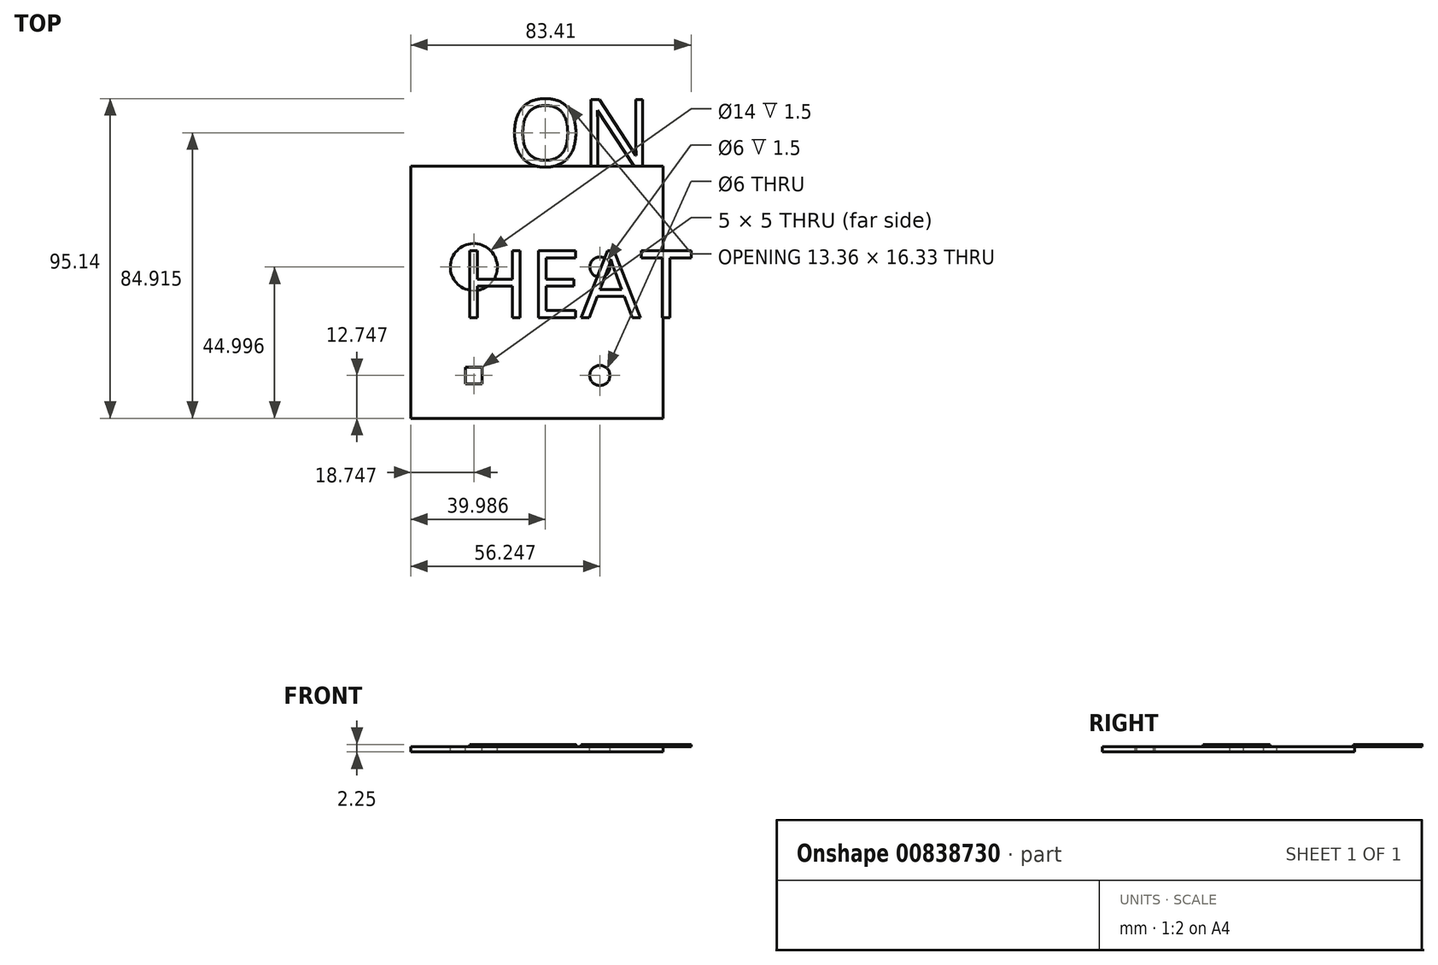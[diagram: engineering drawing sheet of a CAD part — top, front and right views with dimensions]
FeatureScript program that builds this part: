
annotation { "Feature Type Name" : "Feature", "Feature Type Description" : "" }
export const myFeature = defineFeature(function(context is Context, id is Id, definition is map)
    precondition{}
    {
        {
            assignVariable(context, id + "F0", {"name" : "size", "anyValue" : .75});
        }
        {
            var Q0;
            Q0=qCreatedBy(makeId("Top.planeOp"),FACE);
            var sketch = newSketch(context, id + "F1", { "sketchPlane" : qUnion([Q0])});
            skLineSegment(sketch, "E0.bottom", {"start": v(-51.53, 40.36) * mm, "end": v(23.47, 40.36) * mm});
            skLineSegment(sketch, "E0.top", {"start": v(-51.53, -34.64) * mm, "end": v(23.47, -34.64) * mm});
            skLineSegment(sketch, "E0.left", {"start": v(-51.53, 40.36) * mm, "end": v(-51.53, -34.64) * mm});
            skLineSegment(sketch, "E0.right", {"start": v(23.47, 40.36) * mm, "end": v(23.47, -34.64) * mm});
            skSolve(sketch);
        }
        {
            var Q0;
            Q0=makeQuery(id+"F1.imprint","IMPRINT",FACE,{"disambiguationData":[TD([[makeQuery(id+"F1.imprint","IMPRINT",EDGE,{"derivedFrom":sQuery(id+"F1.wireOp",EDGE,"E0.bottom")}),-1.0]])]});
            extrude(context, id + "F2", {"entities" : qUnion([Q0]), "depth" : (getVariable(context, 'size') * 2) * mm, "offsetDistance" : 25 * mm});
        }
        {
            var Q0;
            Q0=makeQuery(id+"F2.opExtrude","CAP_FACE",FACE,{"disambiguationData":[OSD([sQuery(id+"F1.wireOp",EDGE,"E0.bottom"),sQuery(id+"F1.wireOp",EDGE,"E0.top"),sQuery(id+"F1.wireOp",EDGE,"E0.left"),sQuery(id+"F1.wireOp",EDGE,"E0.right")])],"isStart":false});
            var sketch = newSketch(context, id + "F3", { "sketchPlane" : qUnion([Q0])});
            skText(sketch, "E1", { "text": "ON\n", "fontName": "OpenSans-Regular.ttf"});
            skLineSegment(sketch, "E2", {"start": v(-29.65, 29.1) * mm, "end": v(-51.53, 29.1) * mm});
            skLineSegment(sketch, "E3", {"start": v(1.59, 29.1) * mm, "end": v(23.47, 29.1) * mm});
            const initialGuessF3  = {"E1": [-0.02236, 0.04036, 1, 0, 0.02]};
            skSetInitialGuess(sketch, initialGuessF3);
            skSolve(sketch);
        }
        {
            var Q0;
            Q0 = qSketchRegion(id + "F3", true);
            extrude(context, id + "F4", {"entities" : qUnion([Q0]), "operationType" : NewBodyOperationType.ADD, "depth" : (getVariable(context, 'size') * 1) * mm, "offsetDistance" : 25 * mm});
        }
        {
            var Q0;
            {var subQ0=sQuery(id+"F1.wireOp",EDGE,"E0.top");var subQ1=sQuery(id+"F1.wireOp",EDGE,"E0.right");var subQ2=sQuery(id+"F1.wireOp",EDGE,"E0.bottom");var subQ3=sQuery(id+"F1.wireOp",EDGE,"E0.left");Q0=makeQuery(id+"F4.boolean.opBoolean","SPLIT",FACE,{"disambiguationData":[TD([makeQuery(id+"F2.opExtrude","SWEPT_FACE",FACE,{"disambiguationData":[OSD([subQ2])]})])],"derivedFrom":makeQuery(id+"F2.opExtrude","CAP_FACE",FACE,{"disambiguationData":[OSD([subQ2,subQ0,subQ3,subQ1])],"isStart":false})});}
            var sketch = newSketch(context, id + "F5", { "sketchPlane" : qUnion([Q0])});
            skCircle(sketch, "E4", {"center": v(-32.78, 10.36) * mm, "radius": 7 * mm});
            skSolve(sketch);
        }
        {
            var Q0;
            Q0 = qSketchRegion(id + "F5", true);
            extrude(context, id + "F6", {"entities" : qUnion([Q0]), "operationType" : NewBodyOperationType.REMOVE, "oppositeDirection" : true, "depth" : 25 * mm, "offsetDistance" : 25 * mm});
        }
        {
            var Q0;
            {var subQ0=sQuery(id+"F1.wireOp",EDGE,"E0.top");var subQ1=sQuery(id+"F1.wireOp",EDGE,"E0.right");var subQ2=sQuery(id+"F1.wireOp",EDGE,"E0.bottom");var subQ3=sQuery(id+"F1.wireOp",EDGE,"E0.left");Q0=makeQuery(id+"F4.boolean.opBoolean","SPLIT",FACE,{"disambiguationData":[TD([makeQuery(id+"F2.opExtrude","SWEPT_FACE",FACE,{"disambiguationData":[OSD([subQ2])]})])],"derivedFrom":makeQuery(id+"F2.opExtrude","CAP_FACE",FACE,{"disambiguationData":[OSD([subQ2,subQ0,subQ3,subQ1])],"isStart":false})});}
            var sketch = newSketch(context, id + "F7", { "sketchPlane" : qUnion([Q0])});
            skCircle(sketch, "E5.0", {"center": v(-32.78, 10.36) * mm, "radius": 7 * mm});
            skCircle(sketch, "E6", {"center": v(4.72, 10.36) * mm, "radius": 3 * mm});
            skSolve(sketch);
        }
        {
            var Q0;
            Q0 = qSketchRegion(id + "F7", true);
            extrude(context, id + "F8", {"entities" : qUnion([Q0]), "operationType" : NewBodyOperationType.REMOVE, "oppositeDirection" : true, "depth" : 25 * mm, "offsetDistance" : 25 * mm});
        }
        {
            var Q0;
            {var subQ0=sQuery(id+"F1.wireOp",EDGE,"E0.top");var subQ1=sQuery(id+"F1.wireOp",EDGE,"E0.right");var subQ2=sQuery(id+"F1.wireOp",EDGE,"E0.bottom");var subQ3=sQuery(id+"F1.wireOp",EDGE,"E0.left");Q0=makeQuery(id+"F4.boolean.opBoolean","SPLIT",FACE,{"disambiguationData":[TD([makeQuery(id+"F2.opExtrude","SWEPT_FACE",FACE,{"disambiguationData":[OSD([subQ2])]})])],"derivedFrom":makeQuery(id+"F2.opExtrude","CAP_FACE",FACE,{"disambiguationData":[OSD([subQ2,subQ0,subQ3,subQ1])],"isStart":false})});}
            var sketch = newSketch(context, id + "F9", { "sketchPlane" : qUnion([Q0])});
            skText(sketch, "E7", { "text": "HEAT\n", "fontName": "OpenSans-Regular.ttf"});
            skLineSegment(sketch, "E8", {"start": v(-40.44, -7.9) * mm, "end": v(-51.53, -7.9) * mm});
            skLineSegment(sketch, "E9", {"start": v(12.38, -7.9) * mm, "end": v(23.47, -7.9) * mm});
            const initialGuessF9  = {"E7": [-0.03675, -0.00464, 1, 0, 0.02]};
            skSetInitialGuess(sketch, initialGuessF9);
            skSolve(sketch);
        }
        {
            var Q0;
            Q0 = qSketchRegion(id + "F9", true);
            extrude(context, id + "F10", {"entities" : qUnion([Q0]), "operationType" : NewBodyOperationType.ADD, "depth" : (getVariable(context, 'size') * 1) * mm, "offsetDistance" : 25 * mm});
        }
        {
            var Q0;
            {var subQ5=sQuery(id+"F1.wireOp",EDGE,"E0.right");var subQ9=sQuery(id+"F1.wireOp",EDGE,"E0.left");var subQ13=sQuery(id+"F1.wireOp",EDGE,"E0.top");var subQ18=sQuery(id+"F1.wireOp",EDGE,"E0.bottom");var subQ19=makeQuery(id+"F2.opExtrude","SWEPT_FACE",FACE,{"disambiguationData":[OSD([subQ18])]});Q0=makeQuery(id+"F10.boolean.opBoolean","SPLIT",FACE,{"disambiguationData":[TD([subQ19])],"derivedFrom":makeQuery(id+"F4.boolean.opBoolean","SPLIT",FACE,{"disambiguationData":[TD([subQ19])],"derivedFrom":makeQuery(id+"F2.opExtrude","CAP_FACE",FACE,{"disambiguationData":[OSD([subQ18,subQ13,subQ9,subQ5])],"isStart":false})})});}
            var sketch = newSketch(context, id + "F11", { "sketchPlane" : qUnion([Q0])});
            skCircle(sketch, "E10", {"center": v(-32.78, -21.9) * mm, "radius": 5 * mm});
            skCircle(sketch, "E11.0", {"center": v(-32.78, 10.36) * mm, "radius": 7 * mm});
            skCircle(sketch, "E12", {"center": v(4.72, -21.9) * mm, "radius": 3 * mm});
            skCircle(sketch, "E13.0", {"center": v(4.72, 10.36) * mm, "radius": 3 * mm});
            skSolve(sketch);
        }
        {
            var Q0;
            Q0 = qSketchRegion(id + "F11", true);
            extrude(context, id + "F12", {"entities" : qUnion([Q0]), "operationType" : NewBodyOperationType.REMOVE, "oppositeDirection" : true, "depth" : 25 * mm, "offsetDistance" : 25 * mm});
        }
        {
            var Q0;
            {var subQ5=sQuery(id+"F1.wireOp",EDGE,"E0.right");var subQ9=sQuery(id+"F1.wireOp",EDGE,"E0.left");var subQ13=sQuery(id+"F1.wireOp",EDGE,"E0.top");var subQ18=sQuery(id+"F1.wireOp",EDGE,"E0.bottom");var subQ19=makeQuery(id+"F2.opExtrude","SWEPT_FACE",FACE,{"disambiguationData":[OSD([subQ18])]});Q0=makeQuery(id+"F10.boolean.opBoolean","SPLIT",FACE,{"disambiguationData":[TD([subQ19])],"derivedFrom":makeQuery(id+"F4.boolean.opBoolean","SPLIT",FACE,{"disambiguationData":[TD([subQ19])],"derivedFrom":makeQuery(id+"F2.opExtrude","CAP_FACE",FACE,{"disambiguationData":[OSD([subQ18,subQ13,subQ9,subQ5])],"isStart":false})})});}
            var sketch = newSketch(context, id + "F13", { "sketchPlane" : qUnion([Q0])});
            skCircle(sketch, "E14.0", {"center": v(-32.78, -21.9) * mm, "radius": 5 * mm});
            skSolve(sketch);
        }
        {
            var Q0;
            Q0 = qSketchRegion(id + "F13", true);
            var Q1;
            Q1=makeQuery(id+"F2.opExtrude","CAP_FACE",FACE,{"disambiguationData":[OSD([sQuery(id+"F1.wireOp",EDGE,"E0.bottom"),sQuery(id+"F1.wireOp",EDGE,"E0.top"),sQuery(id+"F1.wireOp",EDGE,"E0.left"),sQuery(id+"F1.wireOp",EDGE,"E0.right")])],"isStart":true});
            extrude(context, id + "F14", {"entities" : qUnion([Q0]), "operationType" : NewBodyOperationType.ADD, "endBound" : BoundingType.UP_TO_SURFACE, "oppositeDirection" : true, "depth" : 25 * mm, "endBoundEntityFace" : qUnion([Q1]), "offsetDistance" : 25 * mm});
        }
        {
            var Q0;
            Q0=makeQuery(id+"F13.imprint","IMPRINT",FACE,{"disambiguationData":[TD([[makeQuery(id+"F13.imprint","IMPRINT",EDGE,{"derivedFrom":sQuery(id+"F13.wireOp",EDGE,"E14.0")}),-1.0]])]});
            var sketch = newSketch(context, id + "F15", { "sketchPlane" : qUnion([Q0])});
            skPoint(sketch, "E15.0", {"position": v(-32.78, -21.9) * mm});
            skLineSegment(sketch, "E16.bottom", {"start": v(-30.28, -19.4) * mm, "end": v(-35.28, -19.4) * mm});
            skLineSegment(sketch, "E16.top", {"start": v(-30.28, -24.4) * mm, "end": v(-35.28, -24.4) * mm});
            skLineSegment(sketch, "E16.left", {"start": v(-30.28, -19.4) * mm, "end": v(-30.28, -24.4) * mm});
            skLineSegment(sketch, "E16.right", {"start": v(-35.28, -19.4) * mm, "end": v(-35.28, -24.4) * mm});
            skSolve(sketch);
        }
        {
            var Q0;
            Q0 = qSketchRegion(id + "F15", true);
            extrude(context, id + "F16", {"entities" : qUnion([Q0]), "operationType" : NewBodyOperationType.REMOVE, "oppositeDirection" : true, "depth" : 25 * mm, "offsetDistance" : 25 * mm});
        }
    });
